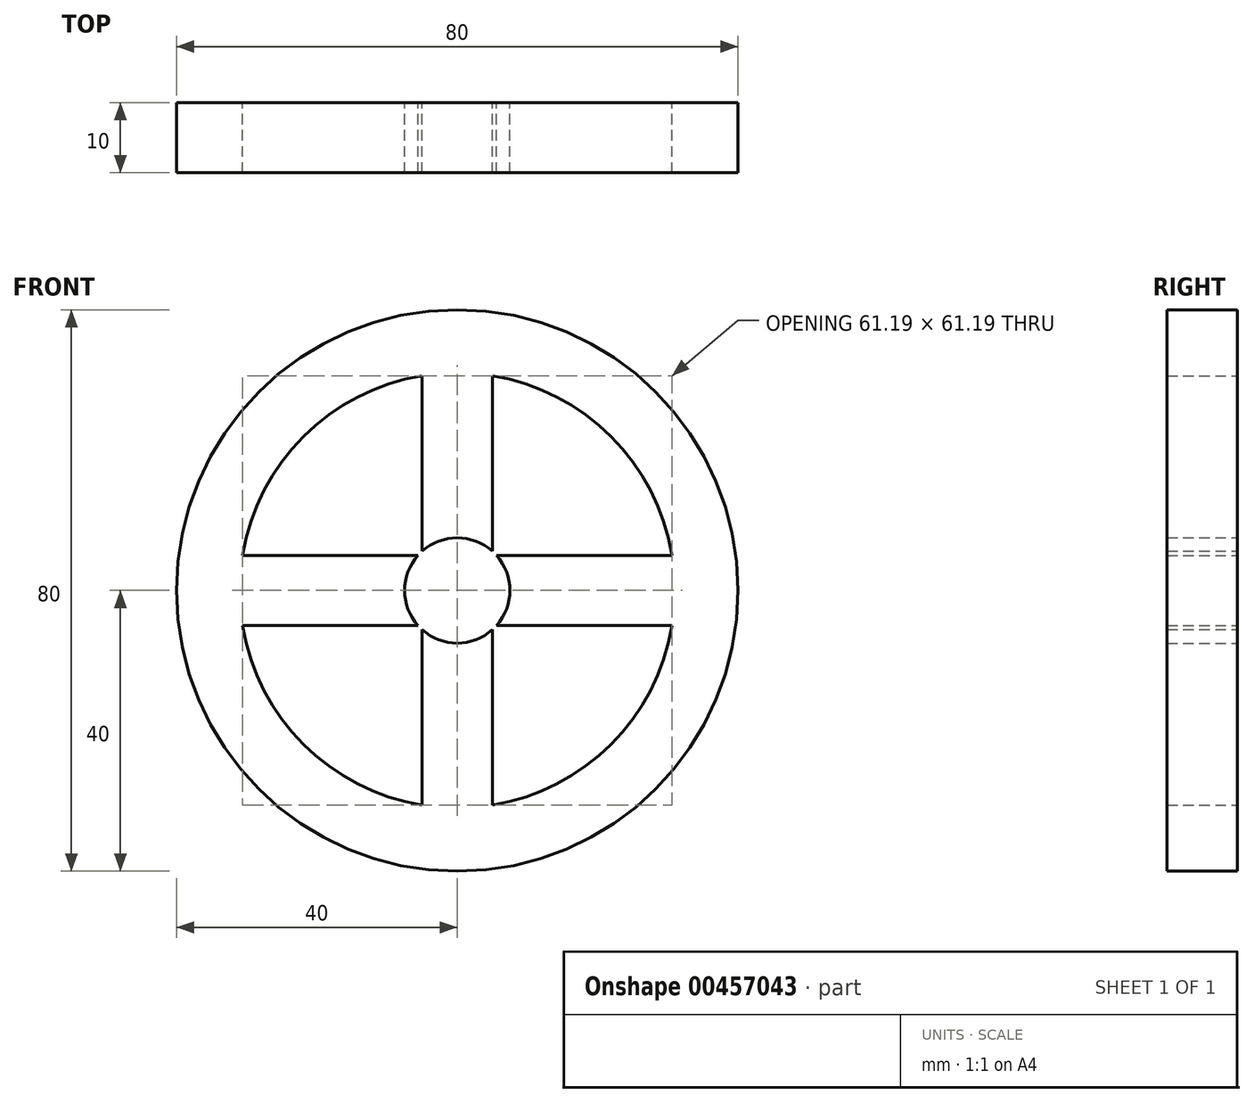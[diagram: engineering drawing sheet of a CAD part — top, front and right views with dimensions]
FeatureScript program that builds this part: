
annotation { "Feature Type Name" : "Feature", "Feature Type Description" : "" }
export const myFeature = defineFeature(function(context is Context, id is Id, definition is map)
    precondition{}
    {
        {
            var Q0;
            Q0=qCreatedBy(makeId("Front.planeOp"),FACE);
            var sketch = newSketch(context, id + "F0", { "sketchPlane" : qUnion([Q0])});
            skCircle(sketch, "E0", {"center": v(0, 0) * mm, "radius": 40 * mm});
            skCircle(sketch, "E1", {"center": v(0, 0) * mm, "radius": 31 * mm});
            skCircle(sketch, "E2", {"center": v(0, 0) * mm, "radius": 7.5 * mm});
            skCircle(sketch, "E3", {"center": v(0, 0) * mm, "radius": 2.5 * mm});
            skLineSegment(sketch, "E4", {"start": v(0, 0) * mm, "end": v(0, 40) * mm});
            skLineSegment(sketch, "E5", {"start": v(0, 0) * mm, "end": v(40, 0) * mm});
            skLineSegment(sketch, "E6", {"start": v(0, 0) * mm, "end": v(-40, 0) * mm});
            skLineSegment(sketch, "E7", {"start": v(0, 0) * mm, "end": v(0, -40) * mm});
            skLineSegment(sketch, "E8.0", {"start": v(5, 0) * mm, "end": v(5, 40) * mm});
            skLineSegment(sketch, "E9.0", {"start": v(-5, 0) * mm, "end": v(-5, 40) * mm});
            skLineSegment(sketch, "E10.0", {"start": v(0, -5) * mm, "end": v(40, -5) * mm});
            skLineSegment(sketch, "E11.0", {"start": v(0, 5) * mm, "end": v(40, 5) * mm});
            skLineSegment(sketch, "E12.0", {"start": v(-5, 0) * mm, "end": v(-5, -40) * mm});
            skLineSegment(sketch, "E13.0", {"start": v(5, 0) * mm, "end": v(5, -40) * mm});
            skLineSegment(sketch, "E14.0", {"start": v(0, 5) * mm, "end": v(-40, 5) * mm});
            skLineSegment(sketch, "E15.0", {"start": v(0, -5) * mm, "end": v(-40, -5) * mm});
            skSolve(sketch);
        }
        {
            var Q0;
            Q0 = qSketchRegion(id + "F0", true);
            var Q1;
            {var subQ0=sQuery(id+"F0.wireOp",EDGE,"E5");var subQ1=sQuery(id+"F0.wireOp",EDGE,"E1");var subQ2=makeQuery(id+"F0.imprint","INTERSECT",VERTEX,{"derivedFrom":[subQ1,subQ0]});Q1=makeQuery(id+"F0.imprint","IMPRINT",FACE,{"disambiguationData":[TD([[makeQuery(id+"F0.imprint","IMPRINT",EDGE,{"disambiguationData":[TD([[subQ2,1.0]])],"derivedFrom":subQ1}),1.0]])]});}
            var Q2;
            {var subQ0=sQuery(id+"F0.wireOp",EDGE,"E11.0");var subQ1=sQuery(id+"F0.wireOp",EDGE,"E1");var subQ2=makeQuery(id+"F0.imprint","INTERSECT",VERTEX,{"derivedFrom":[subQ1,subQ0]});Q2=makeQuery(id+"F0.imprint","IMPRINT",FACE,{"disambiguationData":[TD([[makeQuery(id+"F0.imprint","IMPRINT",EDGE,{"disambiguationData":[TD([[subQ2,1.0]])],"derivedFrom":subQ1}),1.0]])]});}
            var Q3;
            {var subQ0=sQuery(id+"F0.wireOp",EDGE,"E8.0");var subQ1=sQuery(id+"F0.wireOp",EDGE,"E1");var subQ2=makeQuery(id+"F0.imprint","INTERSECT",VERTEX,{"derivedFrom":[subQ1,subQ0]});Q3=makeQuery(id+"F0.imprint","IMPRINT",FACE,{"disambiguationData":[TD([[makeQuery(id+"F0.imprint","IMPRINT",EDGE,{"disambiguationData":[TD([[subQ2,-1.0]])],"derivedFrom":subQ1}),1.0]])]});}
            var Q4;
            {var subQ0=sQuery(id+"F0.wireOp",EDGE,"E4");var subQ1=sQuery(id+"F0.wireOp",EDGE,"E1");var subQ2=makeQuery(id+"F0.imprint","INTERSECT",VERTEX,{"derivedFrom":[subQ1,subQ0]});Q4=makeQuery(id+"F0.imprint","IMPRINT",FACE,{"disambiguationData":[TD([[makeQuery(id+"F0.imprint","IMPRINT",EDGE,{"disambiguationData":[TD([[subQ2,-1.0]])],"derivedFrom":subQ1}),1.0]])]});}
            var Q5;
            {var subQ0=sQuery(id+"F0.wireOp",EDGE,"E14.0");var subQ1=sQuery(id+"F0.wireOp",EDGE,"E1");var subQ2=makeQuery(id+"F0.imprint","INTERSECT",VERTEX,{"derivedFrom":[subQ1,subQ0]});Q5=makeQuery(id+"F0.imprint","IMPRINT",FACE,{"disambiguationData":[TD([[makeQuery(id+"F0.imprint","IMPRINT",EDGE,{"disambiguationData":[TD([[subQ2,-1.0]])],"derivedFrom":subQ1}),1.0]])]});}
            var Q6;
            {var subQ0=sQuery(id+"F0.wireOp",EDGE,"E7");var subQ1=sQuery(id+"F0.wireOp",EDGE,"E1");var subQ2=makeQuery(id+"F0.imprint","INTERSECT",VERTEX,{"derivedFrom":[subQ1,subQ0]});Q6=makeQuery(id+"F0.imprint","IMPRINT",FACE,{"disambiguationData":[TD([[makeQuery(id+"F0.imprint","IMPRINT",EDGE,{"disambiguationData":[TD([[subQ2,-1.0]])],"derivedFrom":subQ1}),1.0]])]});}
            var Q7;
            {var subQ0=sQuery(id+"F0.wireOp",EDGE,"E12.0");var subQ1=sQuery(id+"F0.wireOp",EDGE,"E1");var subQ2=makeQuery(id+"F0.imprint","INTERSECT",VERTEX,{"derivedFrom":[subQ1,subQ0]});Q7=makeQuery(id+"F0.imprint","IMPRINT",FACE,{"disambiguationData":[TD([[makeQuery(id+"F0.imprint","IMPRINT",EDGE,{"disambiguationData":[TD([[subQ2,-1.0]])],"derivedFrom":subQ1}),1.0]])]});}
            var Q8;
            {var subQ0=sQuery(id+"F0.wireOp",EDGE,"E6");var subQ1=sQuery(id+"F0.wireOp",EDGE,"E1");var subQ2=makeQuery(id+"F0.imprint","INTERSECT",VERTEX,{"derivedFrom":[subQ1,subQ0]});Q8=makeQuery(id+"F0.imprint","IMPRINT",FACE,{"disambiguationData":[TD([[makeQuery(id+"F0.imprint","IMPRINT",EDGE,{"disambiguationData":[TD([[subQ2,-1.0]])],"derivedFrom":subQ1}),1.0]])]});}
            extrude(context, id + "F1", {"entities" : qUnion([Q0, Q1, Q2, Q3, Q4, Q5, Q6, Q7, Q8]), "endBound" : BoundingType.SYMMETRIC, "depth" : 10 * mm});
        }
    });
